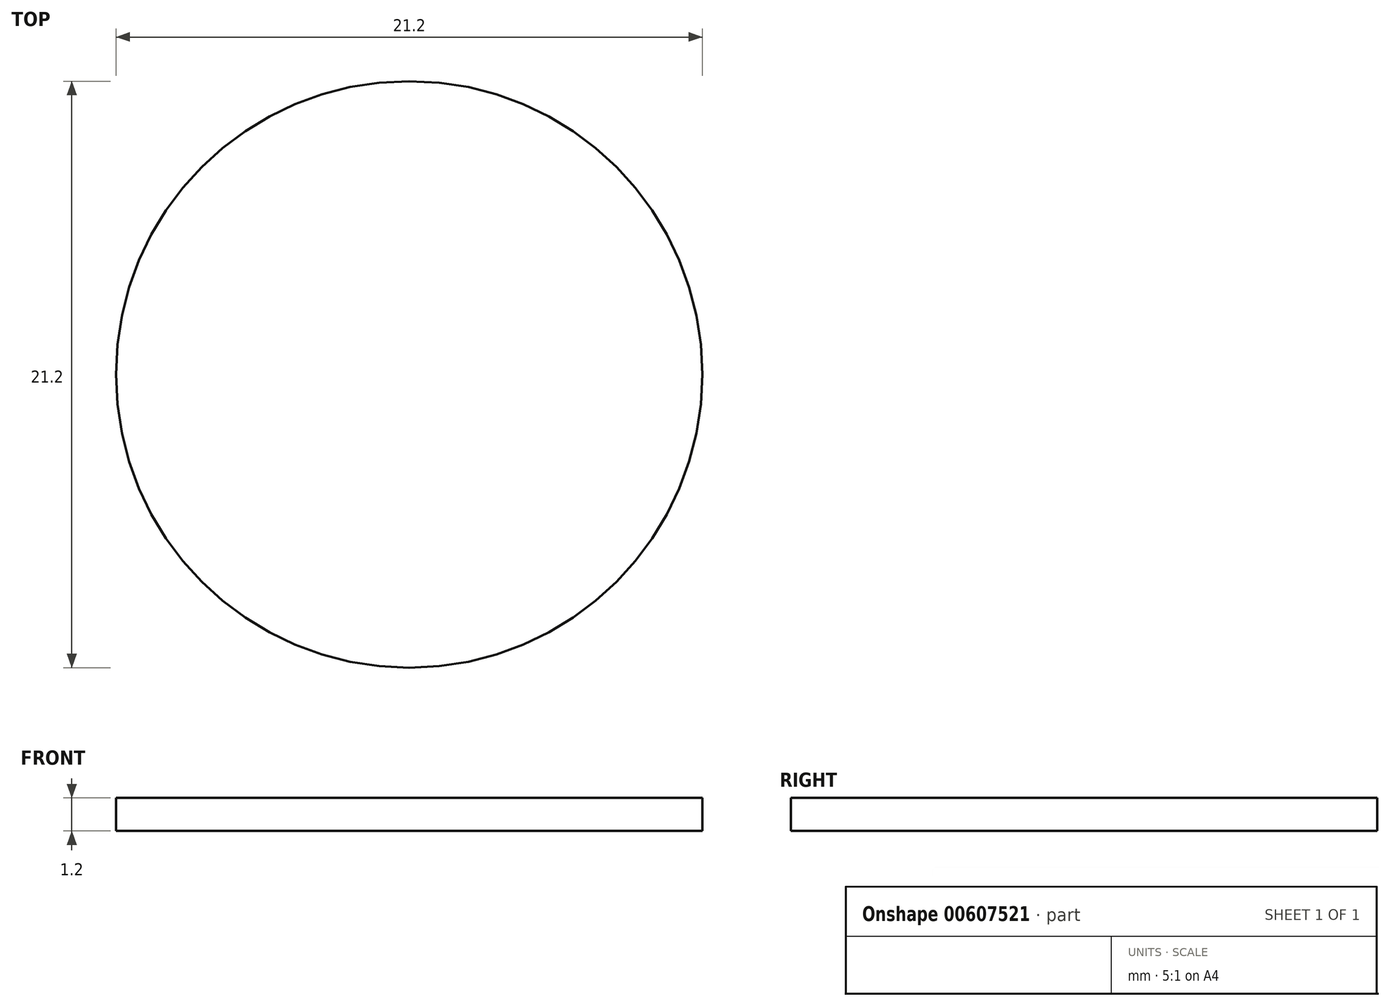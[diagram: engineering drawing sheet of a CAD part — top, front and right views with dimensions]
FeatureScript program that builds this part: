
annotation { "Feature Type Name" : "Feature", "Feature Type Description" : "" }
export const myFeature = defineFeature(function(context is Context, id is Id, definition is map)
    precondition{}
    {
        {
            var Q0;
            Q0=qCreatedBy(makeId("Top.planeOp"),FACE);
            var sketch = newSketch(context, id + "F0", { "sketchPlane" : qUnion([Q0])});
            skCircle(sketch, "E0", {"center": v(0, 0) * mm, "radius": 10.6 * mm});
            skSolve(sketch);
        }
        {
            var Q0;
            Q0 = qSketchRegion(id + "F0", true);
            extrude(context, id + "F1", {"entities" : qUnion([Q0]), "depth" : 1.2 * mm, "offsetDistance" : 25 * mm});
        }
    });
